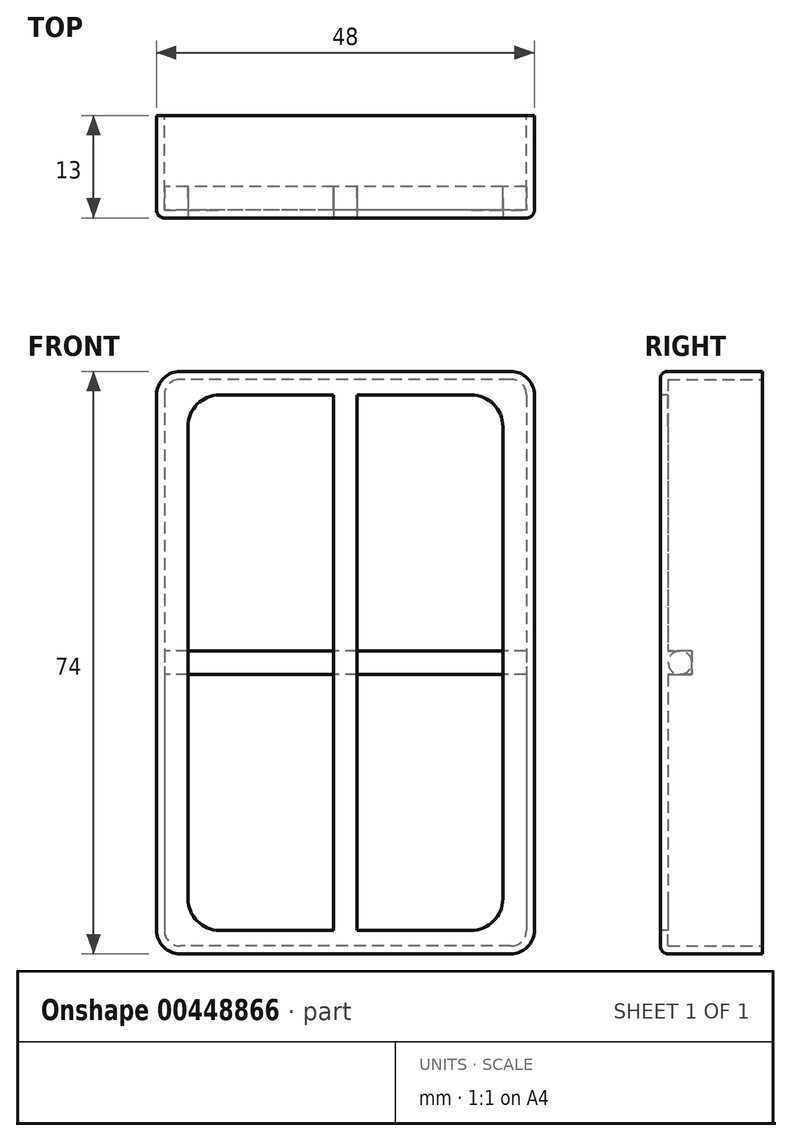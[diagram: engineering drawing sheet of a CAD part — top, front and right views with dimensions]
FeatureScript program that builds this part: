
annotation { "Feature Type Name" : "Feature", "Feature Type Description" : "" }
export const myFeature = defineFeature(function(context is Context, id is Id, definition is map)
    precondition{}
    {
        {
            var Q0;
            Q0=qCreatedBy(makeId("Front.planeOp"),FACE);
            var sketch = newSketch(context, id + "F0", { "sketchPlane" : qUnion([Q0])});
            skLineSegment(sketch, "E0.bottom", {"start": v(21, 37) * mm, "end": v(-21, 37) * mm});
            skLineSegment(sketch, "E0.top", {"start": v(21, -37) * mm, "end": v(-21, -37) * mm});
            skLineSegment(sketch, "E0.left", {"start": v(24, 34) * mm, "end": v(24, -34) * mm});
            skLineSegment(sketch, "E0.right", {"start": v(-24, 34) * mm, "end": v(-24, -34) * mm});
            skPoint(sketch, "E1.visualSharp", {"position": v(24, 37) * mm});
            skArc(sketch, "E1.filletArc", {"start": v(24, 34) * mm, "mid": v(23.12, 36.12) * mm, "end": v(21, 37) * mm});
            skPoint(sketch, "E2.visualSharp", {"position": v(-24, 37) * mm});
            skArc(sketch, "E2.filletArc", {"start": v(-21, 37) * mm, "mid": v(-23.12, 36.12) * mm, "end": v(-24, 34) * mm});
            skPoint(sketch, "E3.visualSharp", {"position": v(-24, -37) * mm});
            skArc(sketch, "E3.filletArc", {"start": v(-24, -34) * mm, "mid": v(-23.12, -36.12) * mm, "end": v(-21, -37) * mm});
            skPoint(sketch, "E4.visualSharp", {"position": v(24, -37) * mm});
            skArc(sketch, "E4.filletArc", {"start": v(21, -37) * mm, "mid": v(23.12, -36.12) * mm, "end": v(24, -34) * mm});
            skSolve(sketch);
        }
        {
            var Q0;
            Q0 = qSketchRegion(id + "F0", true);
            extrude(context, id + "F1", {"entities" : qUnion([Q0]), "depth" : 15.5 * mm, "hasSecondDirection" : true, "secondDirectionOppositeDirection" : false, "secondDirectionDepth" : 2.5 * mm});
        }
        {
            var Q0;
            Q0=makeQuery(id+"F1.opExtrude","CAP_FACE",FACE,{"disambiguationData":[OSD([sQuery(id+"F0.wireOp",EDGE,"E0.bottom"),sQuery(id+"F0.wireOp",EDGE,"E0.top"),sQuery(id+"F0.wireOp",EDGE,"E0.left"),sQuery(id+"F0.wireOp",EDGE,"E0.right"),sQuery(id+"F0.wireOp",EDGE,"E1.filletArc"),sQuery(id+"F0.wireOp",EDGE,"E2.filletArc"),sQuery(id+"F0.wireOp",EDGE,"E3.filletArc"),sQuery(id+"F0.wireOp",EDGE,"E4.filletArc")])],"isStart":true});
            shell(context, id + "F2", {"entities" : qUnion([Q0]), "thickness" : 1 * mm});
        }
        {
            var Q0;
            Q0=makeQuery(id+"F1.opExtrude","CAP_EDGE",EDGE,{"disambiguationData":[OSD([sQuery(id+"F0.wireOp",EDGE,"E0.right")])],"isStart":false});
            fillet(context, id + "F3", {"entities" : qUnion([Q0]), "radius" : 1 * mm, "tangentPropagation" : true, "allowEdgeOverflow" : false});
        }
        {
            var Q0;
            Q0=makeQuery(id+"F1.opExtrude","CAP_FACE",FACE,{"disambiguationData":[OSD([sQuery(id+"F0.wireOp",EDGE,"E0.bottom"),sQuery(id+"F0.wireOp",EDGE,"E0.top"),sQuery(id+"F0.wireOp",EDGE,"E0.left"),sQuery(id+"F0.wireOp",EDGE,"E0.right"),sQuery(id+"F0.wireOp",EDGE,"E1.filletArc"),sQuery(id+"F0.wireOp",EDGE,"E2.filletArc"),sQuery(id+"F0.wireOp",EDGE,"E3.filletArc"),sQuery(id+"F0.wireOp",EDGE,"E4.filletArc")])],"isStart":false});
            var sketch = newSketch(context, id + "F4", { "sketchPlane" : qUnion([Q0])});
            skPoint(sketch, "E5.middle", {"position": v(0, 0.3) * mm});
            skLineSegment(sketch, "E6.0", {"start": v(20, 30) * mm, "end": v(20, -30) * mm});
            skLineSegment(sketch, "E6.1", {"start": v(16, 34) * mm, "end": v(1.5, 34) * mm});
            skLineSegment(sketch, "E6.2", {"start": v(-20, 30) * mm, "end": v(-20, -30) * mm});
            skLineSegment(sketch, "E6.3", {"start": v(16, -34) * mm, "end": v(1.5, -34) * mm});
            skPoint(sketch, "E7.visualSharp", {"position": v(20, 34) * mm});
            skArc(sketch, "E7.filletArc", {"start": v(20, 30) * mm, "mid": v(18.83, 32.83) * mm, "end": v(16, 34) * mm});
            skPoint(sketch, "E8.visualSharp", {"position": v(-20, 34) * mm});
            skArc(sketch, "E8.filletArc", {"start": v(-16, 34) * mm, "mid": v(-18.83, 32.83) * mm, "end": v(-20, 30) * mm});
            skPoint(sketch, "E9.visualSharp", {"position": v(-20, -34) * mm});
            skArc(sketch, "E9.filletArc", {"start": v(-20, -30) * mm, "mid": v(-18.83, -32.83) * mm, "end": v(-16, -34) * mm});
            skPoint(sketch, "E10.visualSharp", {"position": v(20, -34) * mm});
            skArc(sketch, "E10.filletArc", {"start": v(16, -34) * mm, "mid": v(18.83, -32.83) * mm, "end": v(20, -30) * mm});
            skLineSegment(sketch, "E11", {"start": v(1.5, 34) * mm, "end": v(1.5, -34) * mm});
            skLineSegment(sketch, "E12", {"start": v(-1.5, 34) * mm, "end": v(-1.5, -34) * mm});
            skLineSegment(sketch, "E13.trimOffspring", {"start": v(-1.5, 34) * mm, "end": v(-16, 34) * mm});
            skLineSegment(sketch, "E14.trimOffspring", {"start": v(-1.5, -34) * mm, "end": v(-16, -34) * mm});
            skSolve(sketch);
        }
        {
            var Q0;
            Q0 = qSketchRegion(id + "F4", true);
            extrude(context, id + "F5", {"entities" : qUnion([Q0]), "operationType" : NewBodyOperationType.REMOVE, "endBound" : BoundingType.THROUGH_ALL, "oppositeDirection" : true, "depth" : 25 * mm});
        }
        {
            var Q0;
            Q0=qCreatedBy(makeId("Right.planeOp"),FACE);
            var sketch = newSketch(context, id + "F6", { "sketchPlane" : qUnion([Q0])});
            skLineSegment(sketch, "E15.bottom", {"start": v(-11.5, 1.5) * mm, "end": v(-14.5, 1.5) * mm});
            skLineSegment(sketch, "E15.top", {"start": v(-11.5, -1.5) * mm, "end": v(-14.5, -1.5) * mm});
            skLineSegment(sketch, "E15.left", {"start": v(-11.5, 1.5) * mm, "end": v(-11.5, -1.5) * mm});
            skLineSegment(sketch, "E15.right", {"start": v(-14.5, 1.5) * mm, "end": v(-14.5, -1.5) * mm});
            skPoint(sketch, "E15.middle", {"position": v(-13, 0) * mm});
            skSolve(sketch);
        }
        {
            var Q0;
            Q0 = qSketchRegion(id + "F6", true);
            var Q1;
            Q1=makeQuery(id+"F2.opShell","OFFSET_FACE",FACE,{"disambiguationData":[OSD([sQuery(id+"F0.wireOp",EDGE,"E0.left")])]});
            var Q2;
            Q2=makeQuery(id+"F2.opShell","OFFSET_FACE",FACE,{"disambiguationData":[OSD([sQuery(id+"F0.wireOp",EDGE,"E0.right")])]});
            extrude(context, id + "F7", {"entities" : qUnion([Q0]), "operationType" : NewBodyOperationType.ADD, "endBound" : BoundingType.UP_TO_SURFACE, "endBoundEntityFace" : qUnion([Q1]), "depth" : 25 * mm, "hasSecondDirection" : true, "secondDirectionBound" : SecondDirectionBoundingType.UP_TO_SURFACE, "secondDirectionOppositeDirection" : true, "secondDirectionBoundEntityFace" : qUnion([Q2]), "secondDirectionDepth" : 25 * mm});
        }
        {
            var Q0;
            Q0=makeQuery(id+"F5.boolean.opBoolean","COPY",FACE,{"derivedFrom":makeQuery(id+"F5.opExtrude","SWEPT_FACE",FACE,{"disambiguationData":[OSD([sQuery(id+"F4.wireOp",EDGE,"E11")])]})});
            var sketch = newSketch(context, id + "F8", { "sketchPlane" : qUnion([Q0])});
            skCircle(sketch, "E16", {"center": v(-13, 0) * mm, "radius": 1.5 * mm});
            skLineSegment(sketch, "E17.bottom", {"start": v(-11, 2) * mm, "end": v(-15, 2) * mm});
            skLineSegment(sketch, "E17.top", {"start": v(-11, -2) * mm, "end": v(-15, -2) * mm});
            skLineSegment(sketch, "E17.left", {"start": v(-11, 2) * mm, "end": v(-11, -2) * mm});
            skLineSegment(sketch, "E17.right", {"start": v(-15, 2) * mm, "end": v(-15, -2) * mm});
            skSolve(sketch);
        }
        {
            var Q0;
            Q0 = qSketchRegion(id + "F8", true);
            var Q1;
            Q1=makeQuery(id+"F5.boolean.opBoolean","COPY",FACE,{"derivedFrom":makeQuery(id+"F5.opExtrude","SWEPT_FACE",FACE,{"disambiguationData":[OSD([sQuery(id+"F4.wireOp",EDGE,"E6.0")])]})});
            extrude(context, id + "F9", {"entities" : qUnion([Q0]), "operationType" : NewBodyOperationType.REMOVE, "endBound" : BoundingType.UP_TO_SURFACE, "endBoundEntityFace" : qUnion([Q1]), "depth" : 25 * mm});
        }
        {
            var Q0;
            Q0=makeQuery(id+"F5.boolean.opBoolean","COPY",FACE,{"derivedFrom":makeQuery(id+"F5.opExtrude","SWEPT_FACE",FACE,{"disambiguationData":[OSD([sQuery(id+"F4.wireOp",EDGE,"E6.2")])]})});
            var sketch = newSketch(context, id + "F10", { "sketchPlane" : qUnion([Q0])});
            skCircle(sketch, "E18", {"center": v(-13, 0) * mm, "radius": 1.5 * mm});
            skLineSegment(sketch, "E19.bottom", {"start": v(-11, 2) * mm, "end": v(-15, 2) * mm});
            skLineSegment(sketch, "E19.top", {"start": v(-11, -2) * mm, "end": v(-15, -2) * mm});
            skLineSegment(sketch, "E19.left", {"start": v(-11, 2) * mm, "end": v(-11, -2) * mm});
            skLineSegment(sketch, "E19.right", {"start": v(-15, 2) * mm, "end": v(-15, -2) * mm});
            skSolve(sketch);
        }
        {
            var Q0;
            Q0 = qSketchRegion(id + "F10", true);
            var Q1;
            Q1=makeQuery(id+"F5.boolean.opBoolean","COPY",FACE,{"derivedFrom":makeQuery(id+"F5.opExtrude","SWEPT_FACE",FACE,{"disambiguationData":[OSD([sQuery(id+"F4.wireOp",EDGE,"E12")])]})});
            extrude(context, id + "F11", {"entities" : qUnion([Q0]), "operationType" : NewBodyOperationType.REMOVE, "endBound" : BoundingType.UP_TO_SURFACE, "endBoundEntityFace" : qUnion([Q1]), "depth" : 25 * mm});
        }
    });
